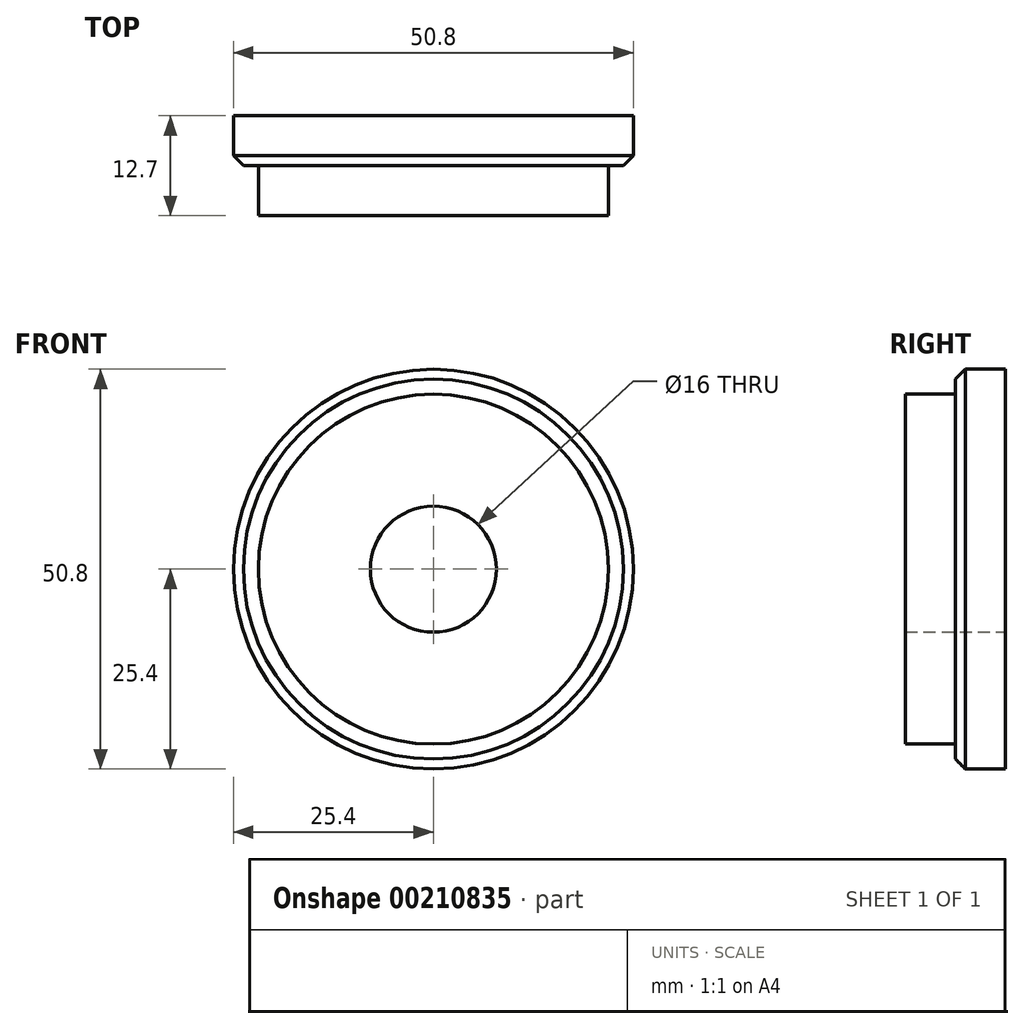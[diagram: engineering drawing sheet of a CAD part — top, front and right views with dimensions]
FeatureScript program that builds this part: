
annotation { "Feature Type Name" : "Feature", "Feature Type Description" : "" }
export const myFeature = defineFeature(function(context is Context, id is Id, definition is map)
    precondition{}
    {
        {
            var Q0;
            Q0=qCreatedBy(makeId("Front.planeOp"),FACE);
            var sketch = newSketch(context, id + "F0", { "sketchPlane" : qUnion([Q0])});
            skCircle(sketch, "E0", {"center": v(0, 0) * mm, "radius": 25.4 * mm});
            skSolve(sketch);
        }
        {
            var Q0;
            Q0=makeQuery(id+"F0.imprint","IMPRINT",FACE,{"disambiguationData":[TD([[makeQuery(id+"F0.imprint","IMPRINT",EDGE,{"derivedFrom":sQuery(id+"F0.wireOp",EDGE,"E0")}),1.0]])]});
            extrude(context, id + "F1", {"entities" : qUnion([Q0]), "depth" : 6.35 * mm});
        }
        {
            var Q0;
            Q0=makeQuery(id+"F1.opExtrude","CAP_FACE",FACE,{"disambiguationData":[OSD([sQuery(id+"F0.wireOp",EDGE,"E0")])],"isStart":false});
            var sketch = newSketch(context, id + "F2", { "sketchPlane" : qUnion([Q0])});
            skCircle(sketch, "E1", {"center": v(0, 0) * mm, "radius": 22.23 * mm});
            skSolve(sketch);
        }
        {
            var Q0;
            Q0=makeQuery(id+"F2.imprint","IMPRINT",FACE,{"disambiguationData":[TD([[makeQuery(id+"F2.imprint","IMPRINT",EDGE,{"derivedFrom":sQuery(id+"F2.wireOp",EDGE,"E1")}),1.0]])]});
            extrude(context, id + "F3", {"entities" : qUnion([Q0]), "operationType" : NewBodyOperationType.ADD, "depth" : 6.35 * mm});
        }
        {
            var Q0;
            Q0=qCreatedBy(makeId("Front.planeOp"),FACE);
            var sketch = newSketch(context, id + "F4", { "sketchPlane" : qUnion([Q0])});
            skCircle(sketch, "E2", {"center": v(0, 0) * mm, "radius": 8 * mm});
            skSolve(sketch);
        }
        {
            var Q0;
            Q0=makeQuery(id+"F4.imprint","IMPRINT",FACE,{"disambiguationData":[TD([[makeQuery(id+"F4.imprint","IMPRINT",EDGE,{"derivedFrom":sQuery(id+"F4.wireOp",EDGE,"E2")}),1.0]])]});
            extrude(context, id + "F5", {"entities" : qUnion([Q0]), "operationType" : NewBodyOperationType.REMOVE, "endBound" : BoundingType.THROUGH_ALL, "depth" : 25.4 * mm});
        }
        {
            var Q0;
            Q0=makeQuery(id+"F1.opExtrude","CAP_EDGE",EDGE,{"disambiguationData":[OSD([sQuery(id+"F0.wireOp",EDGE,"E0")])],"isStart":false});
            chamfer(context, id + "F6", {"entities" : qUnion([Q0]), "width" : 1.27 * mm, "tangentPropagation" : true});
        }
    });
